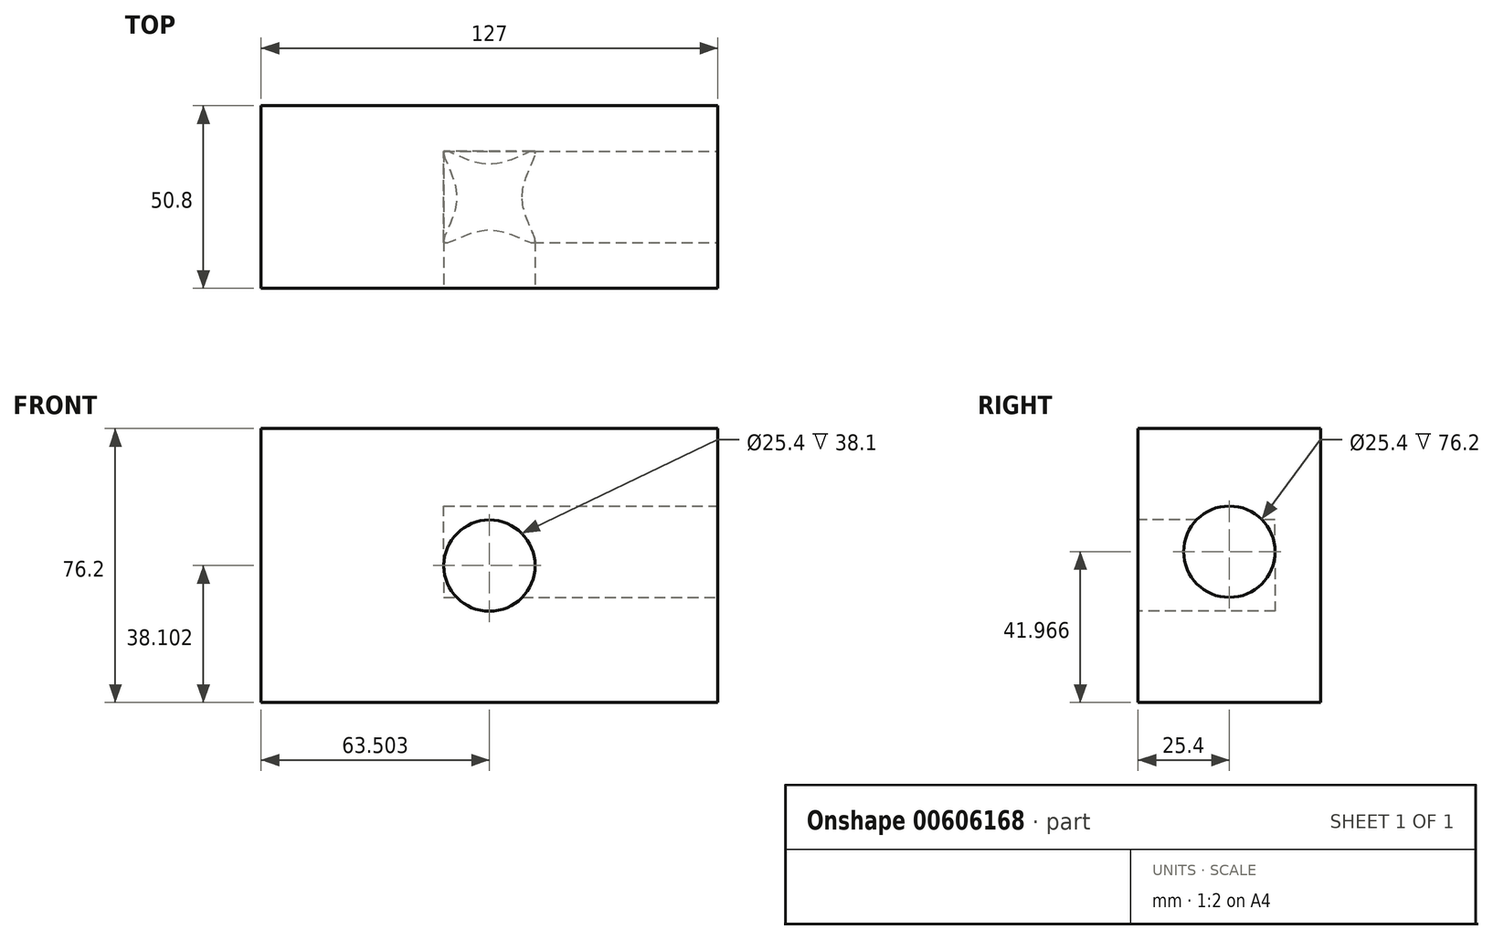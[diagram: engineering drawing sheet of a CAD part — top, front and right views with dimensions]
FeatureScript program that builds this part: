
annotation { "Feature Type Name" : "Feature", "Feature Type Description" : "" }
export const myFeature = defineFeature(function(context is Context, id is Id, definition is map)
    precondition{}
    {
        {
            var Q0;
            Q0=qCreatedBy(makeId("Front.planeOp"),FACE);
            var sketch = newSketch(context, id + "F0", { "sketchPlane" : qUnion([Q0])});
            skLineSegment(sketch, "E0.bottom", {"start": v(-73.75, 21.65) * mm, "end": v(53.25, 21.65) * mm});
            skLineSegment(sketch, "E0.top", {"start": v(-73.75, -54.55) * mm, "end": v(53.25, -54.55) * mm});
            skLineSegment(sketch, "E0.left", {"start": v(-73.75, 21.65) * mm, "end": v(-73.75, -54.55) * mm});
            skLineSegment(sketch, "E0.right", {"start": v(53.25, 21.65) * mm, "end": v(53.25, -54.55) * mm});
            skSolve(sketch);
        }
        {
            var Q0;
            Q0 = qSketchRegion(id + "F0", true);
            extrude(context, id + "F1", {"entities" : qUnion([Q0]), "depth" : 50.8 * mm, "offsetDistance" : 25.4 * mm});
        }
        {
            var Q0;
            Q0=makeQuery(id+"F1.opExtrude","CAP_FACE",FACE,{"disambiguationData":[OSD([sQuery(id+"F0.wireOp",EDGE,"E0.bottom"),sQuery(id+"F0.wireOp",EDGE,"E0.top"),sQuery(id+"F0.wireOp",EDGE,"E0.left"),sQuery(id+"F0.wireOp",EDGE,"E0.right")])],"isStart":false});
            var sketch = newSketch(context, id + "F2", { "sketchPlane" : qUnion([Q0])});
            skCircle(sketch, "E1", {"center": v(-10.25, -16.45) * mm, "radius": 12.7 * mm});
            skSolve(sketch);
        }
        {
            var Q0;
            Q0=makeQuery(id+"F2.imprint","IMPRINT",FACE,{"disambiguationData":[TD([[makeQuery(id+"F2.imprint","IMPRINT",EDGE,{"derivedFrom":sQuery(id+"F2.wireOp",EDGE,"E1")}),1.0]])]});
            extrude(context, id + "F3", {"entities" : qUnion([Q0]), "operationType" : NewBodyOperationType.REMOVE, "oppositeDirection" : true, "depth" : 38.1 * mm, "offsetDistance" : 25.4 * mm});
        }
        {
            var Q0;
            Q0=makeQuery(id+"F1.opExtrude","SWEPT_FACE",FACE,{"disambiguationData":[OSD([sQuery(id+"F0.wireOp",EDGE,"E0.right")])]});
            var sketch = newSketch(context, id + "F4", { "sketchPlane" : qUnion([Q0])});
            skCircle(sketch, "E2", {"center": v(-25.4, -12.58) * mm, "radius": 12.7 * mm});
            skSolve(sketch);
        }
        {
            var Q0;
            Q0=makeQuery(id+"F4.imprint","IMPRINT",FACE,{"disambiguationData":[TD([[makeQuery(id+"F4.imprint","IMPRINT",EDGE,{"derivedFrom":sQuery(id+"F4.wireOp",EDGE,"E2")}),1.0]])]});
            var Q1;
            Q1=sQuery(id+"F4.wireOp",EDGE,"E2");
            extrude(context, id + "F5", {"entities" : qUnion([Q0]), "operationType" : NewBodyOperationType.REMOVE, "surfaceEntities" : qUnion([Q1]), "oppositeDirection" : true, "depth" : 76.2 * mm, "offsetDistance" : 25.4 * mm});
        }
    });
